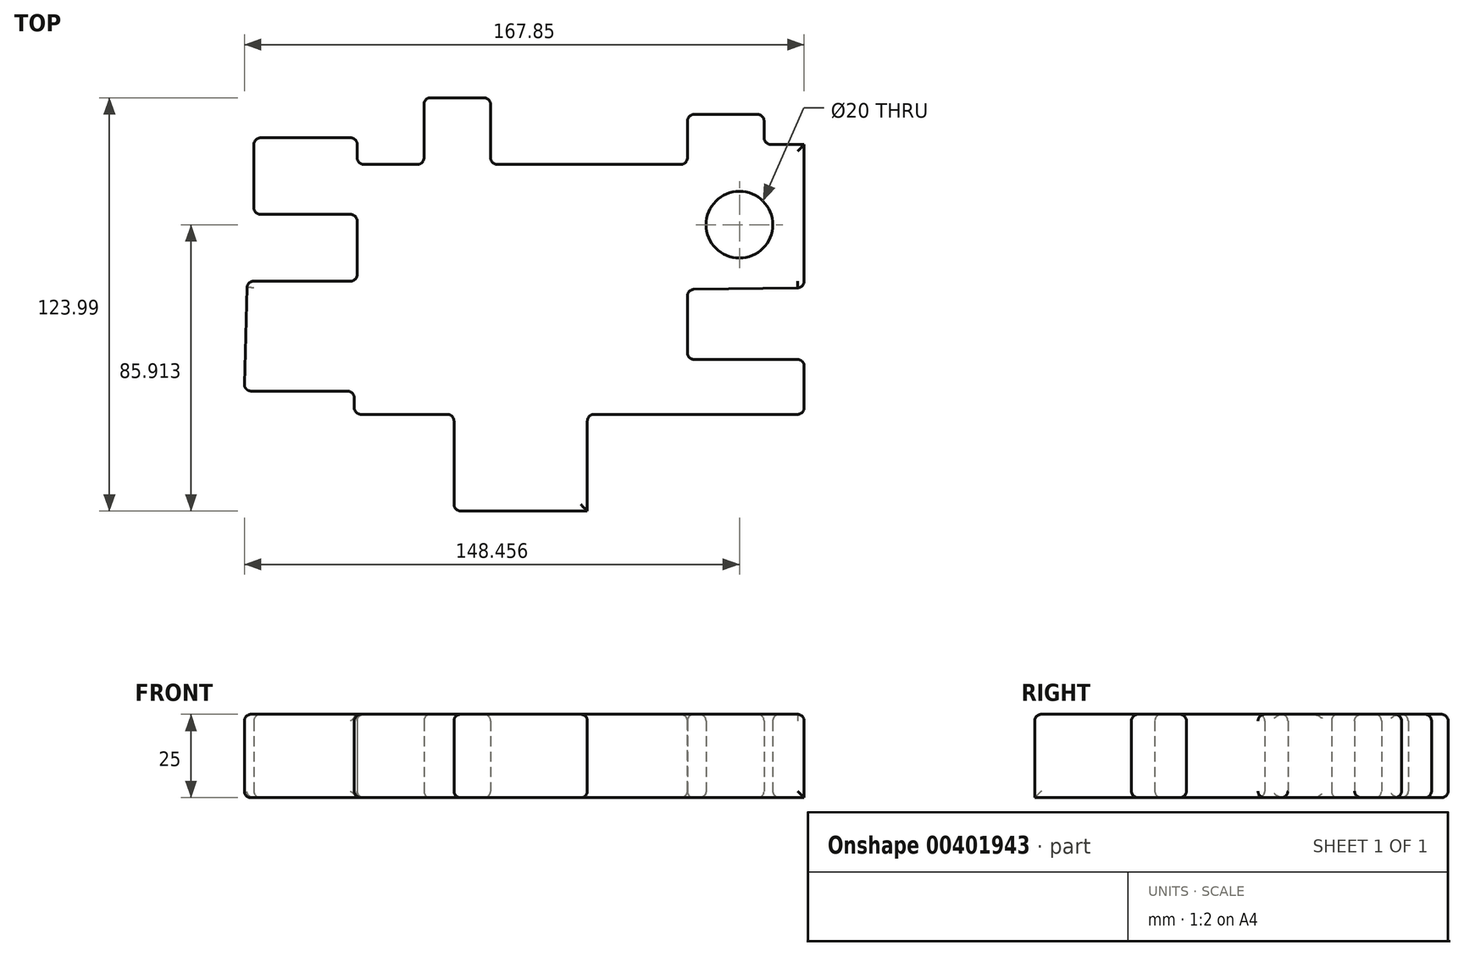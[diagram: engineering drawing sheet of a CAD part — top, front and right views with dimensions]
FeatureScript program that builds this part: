
annotation { "Feature Type Name" : "Feature", "Feature Type Description" : "" }
export const myFeature = defineFeature(function(context is Context, id is Id, definition is map)
    precondition{}
    {
        {
            var Q0;
            Q0=qCreatedBy(makeId("Top.planeOp"),FACE);
            var sketch = newSketch(context, id + "F0", { "sketchPlane" : qUnion([Q0])});
            skLineSegment(sketch, "E0.bottom", {"start": v(-24.1, 37.5) * mm, "end": v(34.9, 37.5) * mm});
            skLineSegment(sketch, "E0.top", {"start": v(-45.1, -37.49) * mm, "end": v(-35.1, -37.49) * mm});
            skLineSegment(sketch, "E1.bottom", {"start": v(-64.1, 2.5) * mm, "end": v(-97.1, 2.5) * mm});
            skLineSegment(sketch, "E1.top", {"start": v(-65.01, -30.49) * mm, "end": v(-98.01, -30.49) * mm});
            skLineSegment(sketch, "E1.right", {"start": v(-97.1, 2.5) * mm, "end": v(-98.01, -30.49) * mm});
            skLineSegment(sketch, "E2.top", {"start": v(-64.1, 37.5) * mm, "end": v(-44.1, 37.5) * mm});
            skLineSegment(sketch, "E2.left", {"start": v(-64.1, 2.5) * mm, "end": v(-64.1, 37.5) * mm});
            skLineSegment(sketch, "E3.top", {"start": v(-65.01, -37.49) * mm, "end": v(-45.1, -37.49) * mm});
            skLineSegment(sketch, "E3.left", {"start": v(-65.01, -30.49) * mm, "end": v(-65.01, -37.49) * mm});
            skLineSegment(sketch, "E4.bottom", {"start": v(34.9, -37.49) * mm, "end": v(69.9, -37.49) * mm});
            skLineSegment(sketch, "E4.top", {"start": v(34.9, -21) * mm, "end": v(69.9, -21) * mm});
            skLineSegment(sketch, "E4.right", {"start": v(69.9, -37.49) * mm, "end": v(69.9, -21) * mm});
            skLineSegment(sketch, "E5.bottom", {"start": v(34.9, 0) * mm, "end": v(69.9, 0.5) * mm});
            skLineSegment(sketch, "E6.top", {"start": v(69.9, 43.5) * mm, "end": v(57.9, 43.5) * mm});
            skLineSegment(sketch, "E6.left", {"start": v(69.9, 37.5) * mm, "end": v(69.9, 43.5) * mm});
            skLineSegment(sketch, "E7.top", {"start": v(-44.1, 57.5) * mm, "end": v(-24.1, 57.5) * mm});
            skLineSegment(sketch, "E7.left", {"start": v(-44.1, 37.5) * mm, "end": v(-44.1, 57.5) * mm});
            skLineSegment(sketch, "E7.right", {"start": v(-24.1, 37.5) * mm, "end": v(-24.1, 57.5) * mm});
            skLineSegment(sketch, "E8.top", {"start": v(34.9, 52.5) * mm, "end": v(57.9, 52.5) * mm});
            skLineSegment(sketch, "E8.left", {"start": v(34.9, 37.5) * mm, "end": v(34.9, 52.5) * mm});
            skLineSegment(sketch, "E8.right", {"start": v(57.9, 43.5) * mm, "end": v(57.9, 52.5) * mm});
            skLineSegment(sketch, "E9.top", {"start": v(-35.1, -66.49) * mm, "end": v(4.9, -66.49) * mm});
            skLineSegment(sketch, "E9.left", {"start": v(-35.1, -37.49) * mm, "end": v(-35.1, -66.49) * mm});
            skLineSegment(sketch, "E9.right", {"start": v(4.9, -37.49) * mm, "end": v(4.9, -57.49) * mm});
            skLineSegment(sketch, "E10.bottom", {"start": v(4.9, -66.49) * mm, "end": v(24.9, -66.49) * mm});
            skLineSegment(sketch, "E10.top", {"start": v(4.9, -66.49) * mm, "end": v(24.9, -66.49) * mm});
            skLineSegment(sketch, "E10.left", {"start": v(4.9, -66.49) * mm, "end": v(4.9, -66.49) * mm});
            skLineSegment(sketch, "E10.right", {"start": v(24.9, -66.49) * mm, "end": v(24.9, -66.49) * mm});
            skLineSegment(sketch, "E11.bottom", {"start": v(24.9, -57.49) * mm, "end": v(24.9, -57.49) * mm});
            skLineSegment(sketch, "E11.left", {"start": v(24.9, -57.49) * mm, "end": v(24.9, -66.49) * mm});
            skLineSegment(sketch, "E11.right", {"start": v(24.9, -57.49) * mm, "end": v(24.9, -66.49) * mm});
            skLineSegment(sketch, "E12.bottom", {"start": v(24.9, -57.49) * mm, "end": v(4.9, -57.49) * mm});
            skLineSegment(sketch, "E12.top", {"start": v(24.9, -57.49) * mm, "end": v(4.9, -57.49) * mm});
            skLineSegment(sketch, "E12.right", {"start": v(4.9, -57.49) * mm, "end": v(4.9, -57.49) * mm});
            skLineSegment(sketch, "E13.trimOffspring", {"start": v(4.9, -37.49) * mm, "end": v(34.9, -37.49) * mm});
            skLineSegment(sketch, "E14.trimOffspring", {"start": v(34.9, 0) * mm, "end": v(34.9, -21) * mm});
            skLineSegment(sketch, "E15", {"start": v(-64.1, 2.5) * mm, "end": v(-65.01, -30.49) * mm});
            skLineSegment(sketch, "E16", {"start": v(-44.1, 37.5) * mm, "end": v(-44.1, 2.5) * mm});
            skLineSegment(sketch, "E17", {"start": v(-44.1, 2.5) * mm, "end": v(-64.1, 2.5) * mm});
            skLineSegment(sketch, "E18", {"start": v(-44.1, 37.5) * mm, "end": v(-24.1, 37.5) * mm});
            skLineSegment(sketch, "E19", {"start": v(-44.1, 2.5) * mm, "end": v(-45.1, -37.49) * mm});
            skLineSegment(sketch, "E20", {"start": v(-35.1, -37.49) * mm, "end": v(4.9, -37.49) * mm});
            skLineSegment(sketch, "E21", {"start": v(4.9, -57.49) * mm, "end": v(4.9, -66.49) * mm});
            skLineSegment(sketch, "E22", {"start": v(34.4, -17.5) * mm, "end": v(34.9, -37.49) * mm});
            skLineSegment(sketch, "E23", {"start": v(34.9, 37.5) * mm, "end": v(57.9, 37.5) * mm});
            skLineSegment(sketch, "E24", {"start": v(57.9, 37.5) * mm, "end": v(57.9, 43.5) * mm});
            skLineSegment(sketch, "E25", {"start": v(34.9, 0) * mm, "end": v(34.9, 37.5) * mm});
            skLineSegment(sketch, "E26", {"start": v(57.9, 37.5) * mm, "end": v(69.9, 37.5) * mm});
            skLineSegment(sketch, "E27.bottom", {"start": v(-64.1, 22.5) * mm, "end": v(-95.1, 22.5) * mm});
            skLineSegment(sketch, "E27.top", {"start": v(-64.1, 45.5) * mm, "end": v(-95.1, 45.5) * mm});
            skLineSegment(sketch, "E27.left", {"start": v(-64.1, 22.5) * mm, "end": v(-64.1, 45.5) * mm});
            skLineSegment(sketch, "E27.right", {"start": v(-95.1, 22.5) * mm, "end": v(-95.1, 45.5) * mm});
            skLineSegment(sketch, "E28", {"start": v(-64.1, 45.5) * mm, "end": v(-64.1, 37.5) * mm});
            skLineSegment(sketch, "E29", {"start": v(-64.1, 22.5) * mm, "end": v(-64.1, 2.5) * mm});
            skPoint(sketch, "E30.orphan", {"position": v(69.9, 27.5) * mm});
            skLineSegment(sketch, "E31", {"start": v(69.9, 37.5) * mm, "end": v(69.9, 0.5) * mm});
            skCircle(sketch, "E32", {"center": v(50.5, 19.42) * mm, "radius": 10 * mm});
            skSolve(sketch);
        }
        {
            var Q0;
            Q0=makeQuery(id+"F0.imprint","IMPRINT",FACE,{"disambiguationData":[TD([[makeQuery(id+"F0.imprint","IMPRINT",EDGE,{"derivedFrom":sQuery(id+"F0.wireOp",EDGE,"E0.bottom")}),-1.0]])]});
            var Q1;
            Q1=makeQuery(id+"F0.imprint","IMPRINT",FACE,{"disambiguationData":[TD([[makeQuery(id+"F0.imprint","IMPRINT",EDGE,{"derivedFrom":sQuery(id+"F0.wireOp",EDGE,"E2.top")}),-1.0]])]});
            var Q2;
            Q2=makeQuery(id+"F0.imprint","IMPRINT",FACE,{"disambiguationData":[TD([[makeQuery(id+"F0.imprint","IMPRINT",EDGE,{"derivedFrom":sQuery(id+"F0.wireOp",EDGE,"E27.bottom")}),-1.0]])]});
            var Q3;
            Q3=makeQuery(id+"F0.imprint","IMPRINT",FACE,{"disambiguationData":[TD([[makeQuery(id+"F0.imprint","IMPRINT",EDGE,{"derivedFrom":sQuery(id+"F0.wireOp",EDGE,"E7.top")}),-1.0]])]});
            var Q4;
            Q4=makeQuery(id+"F0.imprint","IMPRINT",FACE,{"disambiguationData":[TD([[makeQuery(id+"F0.imprint","IMPRINT",EDGE,{"derivedFrom":sQuery(id+"F0.wireOp",EDGE,"E3.top")}),1.0]])]});
            var Q5;
            Q5=makeQuery(id+"F0.imprint","IMPRINT",FACE,{"disambiguationData":[TD([[makeQuery(id+"F0.imprint","IMPRINT",EDGE,{"derivedFrom":sQuery(id+"F0.wireOp",EDGE,"E1.bottom")}),1.0]])]});
            var Q6;
            Q6=makeQuery(id+"F0.imprint","IMPRINT",FACE,{"disambiguationData":[TD([[makeQuery(id+"F0.imprint","IMPRINT",EDGE,{"derivedFrom":sQuery(id+"F0.wireOp",EDGE,"E9.top")}),1.0]])]});
            var Q7;
            Q7=makeQuery(id+"F0.imprint","IMPRINT",FACE,{"disambiguationData":[TD([[makeQuery(id+"F0.imprint","IMPRINT",EDGE,{"derivedFrom":sQuery(id+"F0.wireOp",EDGE,"E10.top")}),1.0]])]});
            var Q8;
            Q8=makeQuery(id+"F0.imprint","IMPRINT",FACE,{"disambiguationData":[TD([[makeQuery(id+"F0.imprint","IMPRINT",EDGE,{"derivedFrom":sQuery(id+"F0.wireOp",EDGE,"E5.bottom")}),1.0]])]});
            var Q9;
            Q9=makeQuery(id+"F0.imprint","IMPRINT",FACE,{"disambiguationData":[TD([[makeQuery(id+"F0.imprint","IMPRINT",EDGE,{"derivedFrom":sQuery(id+"F0.wireOp",EDGE,"E8.top")}),-1.0]])]});
            var Q10;
            {var subQ0=sQuery(id+"F0.wireOp",EDGE,"E6.top");Q10=makeQuery(id+"F0.imprint","IMPRINT",FACE,{"disambiguationData":[TD([[makeQuery(id+"F0.imprint","IMPRINT",EDGE,{"derivedFrom":subQ0}),1.0]])]});}
            extrude(context, id + "F1", {"entities" : qUnion([Q0, Q1, Q2, Q3, Q4, Q5, Q6, Q7, Q8, Q9, Q10]), "depth" : 25 * mm});
        }
        {
            var Q0;
            Q0=makeQuery(id+"F1.opExtrude","CAP_EDGE",EDGE,{"disambiguationData":[OSD([sQuery(id+"F0.wireOp",EDGE,"E7.left")])],"isStart":false});
            var Q1;
            Q1=makeQuery(id+"F1.opExtrude","CAP_EDGE",EDGE,{"disambiguationData":[OSD([sQuery(id+"F0.wireOp",EDGE,"E7.top")])],"isStart":false});
            var Q2;
            Q2=makeQuery(id+"F1.opExtrude","CAP_EDGE",EDGE,{"disambiguationData":[OSD([sQuery(id+"F0.wireOp",EDGE,"E7.right")])],"isStart":false});
            var Q3;
            Q3=makeQuery(id+"F1.opExtrude","CAP_EDGE",EDGE,{"disambiguationData":[OSD([sQuery(id+"F0.wireOp",EDGE,"E0.bottom")])],"isStart":false});
            var Q4;
            Q4=makeQuery(id+"F1.opExtrude","CAP_EDGE",EDGE,{"disambiguationData":[OSD([sQuery(id+"F0.wireOp",EDGE,"E8.left")])],"isStart":false});
            var Q5;
            Q5=makeQuery(id+"F1.opExtrude","CAP_EDGE",EDGE,{"disambiguationData":[OSD([sQuery(id+"F0.wireOp",EDGE,"E8.top")])],"isStart":false});
            var Q6;
            Q6=makeQuery(id+"F1.opExtrude","CAP_EDGE",EDGE,{"disambiguationData":[OSD([sQuery(id+"F0.wireOp",EDGE,"E8.right")])],"isStart":false});
            var Q7;
            Q7=makeQuery(id+"F1.opExtrude","CAP_EDGE",EDGE,{"disambiguationData":[OSD([sQuery(id+"F0.wireOp",EDGE,"E6.top")])],"isStart":false});
            var Q8;
            Q8=makeQuery(id+"F1.opExtrude","CAP_EDGE",EDGE,{"disambiguationData":[OSD([sQuery(id+"F0.wireOp",EDGE,"E6.left")])],"isStart":false});
            var Q9;
            Q9=makeQuery(id+"F1.opExtrude","CAP_EDGE",EDGE,{"disambiguationData":[OSD([sQuery(id+"F0.wireOp",EDGE,"E5.right")])],"isStart":false});
            var Q10;
            Q10=makeQuery(id+"F1.opExtrude","CAP_EDGE",EDGE,{"disambiguationData":[OSD([sQuery(id+"F0.wireOp",EDGE,"E5.bottom")])],"isStart":false});
            var Q11;
            Q11=makeQuery(id+"F1.opExtrude","CAP_EDGE",EDGE,{"disambiguationData":[OSD([sQuery(id+"F0.wireOp",EDGE,"E14.trimOffspring")])],"isStart":false});
            var Q12;
            Q12=makeQuery(id+"F1.opExtrude","CAP_EDGE",EDGE,{"disambiguationData":[OSD([sQuery(id+"F0.wireOp",EDGE,"E4.top")])],"isStart":false});
            var Q13;
            Q13=makeQuery(id+"F1.opExtrude","CAP_EDGE",EDGE,{"disambiguationData":[OSD([sQuery(id+"F0.wireOp",EDGE,"E4.right")])],"isStart":false});
            var Q14;
            Q14=makeQuery(id+"F1.opExtrude","CAP_EDGE",EDGE,{"disambiguationData":[OSD([sQuery(id+"F0.wireOp",EDGE,"E4.bottom"),sQuery(id+"F0.wireOp",EDGE,"E13.trimOffspring")])],"isStart":false});
            var Q15;
            Q15=makeQuery(id+"F1.opExtrude","CAP_EDGE",EDGE,{"disambiguationData":[OSD([sQuery(id+"F0.wireOp",EDGE,"E9.right")])],"isStart":false});
            var Q16;
            Q16=makeQuery(id+"F1.opExtrude","CAP_EDGE",EDGE,{"disambiguationData":[OSD([sQuery(id+"F0.wireOp",EDGE,"E12.top")])],"isStart":false});
            var Q17;
            Q17=makeQuery(id+"F1.opExtrude","CAP_EDGE",EDGE,{"disambiguationData":[OSD([sQuery(id+"F0.wireOp",EDGE,"E11.right")])],"isStart":false});
            var Q18;
            Q18=makeQuery(id+"F1.opExtrude","CAP_EDGE",EDGE,{"disambiguationData":[OSD([sQuery(id+"F0.wireOp",EDGE,"E9.top"),sQuery(id+"F0.wireOp",EDGE,"E10.top")])],"isStart":false});
            var Q19;
            Q19=makeQuery(id+"F1.opExtrude","CAP_EDGE",EDGE,{"disambiguationData":[OSD([sQuery(id+"F0.wireOp",EDGE,"E9.left")])],"isStart":false});
            var Q20;
            Q20=makeQuery(id+"F1.opExtrude","CAP_EDGE",EDGE,{"disambiguationData":[OSD([sQuery(id+"F0.wireOp",EDGE,"E0.top"),sQuery(id+"F0.wireOp",EDGE,"E3.top")])],"isStart":false});
            var Q21;
            Q21=makeQuery(id+"F1.opExtrude","CAP_EDGE",EDGE,{"disambiguationData":[OSD([sQuery(id+"F0.wireOp",EDGE,"E3.left")])],"isStart":false});
            var Q22;
            Q22=makeQuery(id+"F1.opExtrude","CAP_EDGE",EDGE,{"disambiguationData":[OSD([sQuery(id+"F0.wireOp",EDGE,"E1.top")])],"isStart":false});
            var Q23;
            Q23=makeQuery(id+"F1.opExtrude","CAP_EDGE",EDGE,{"disambiguationData":[OSD([sQuery(id+"F0.wireOp",EDGE,"E1.right")])],"isStart":false});
            var Q24;
            Q24=makeQuery(id+"F1.opExtrude","CAP_EDGE",EDGE,{"disambiguationData":[OSD([sQuery(id+"F0.wireOp",EDGE,"E1.bottom")])],"isStart":false});
            var Q25;
            Q25=makeQuery(id+"F1.opExtrude","CAP_EDGE",EDGE,{"disambiguationData":[OSD([sQuery(id+"F0.wireOp",EDGE,"E29")])],"isStart":false});
            var Q26;
            Q26=makeQuery(id+"F1.opExtrude","CAP_EDGE",EDGE,{"disambiguationData":[OSD([sQuery(id+"F0.wireOp",EDGE,"E27.bottom")])],"isStart":false});
            var Q27;
            Q27=makeQuery(id+"F1.opExtrude","CAP_EDGE",EDGE,{"disambiguationData":[OSD([sQuery(id+"F0.wireOp",EDGE,"E27.right")])],"isStart":false});
            var Q28;
            Q28=makeQuery(id+"F1.opExtrude","CAP_EDGE",EDGE,{"disambiguationData":[OSD([sQuery(id+"F0.wireOp",EDGE,"E27.top")])],"isStart":false});
            var Q29;
            Q29=makeQuery(id+"F1.opExtrude","CAP_EDGE",EDGE,{"disambiguationData":[OSD([sQuery(id+"F0.wireOp",EDGE,"E28")])],"isStart":false});
            var Q30;
            Q30=makeQuery(id+"F1.opExtrude","CAP_EDGE",EDGE,{"disambiguationData":[OSD([sQuery(id+"F0.wireOp",EDGE,"E2.top")])],"isStart":false});
            var Q31;
            Q31=makeQuery(id+"F1.opExtrude","CAP_EDGE",EDGE,{"disambiguationData":[OSD([sQuery(id+"F0.wireOp",EDGE,"E31")])],"isStart":false});
            var Q32;
            Q32=makeQuery(id+"F1.opExtrude","CAP_EDGE",EDGE,{"disambiguationData":[OSD([sQuery(id+"F0.wireOp",EDGE,"E7.top")])],"isStart":true});
            var Q33;
            Q33=makeQuery(id+"F1.opExtrude","CAP_EDGE",EDGE,{"disambiguationData":[OSD([sQuery(id+"F0.wireOp",EDGE,"E7.right")])],"isStart":true});
            var Q34;
            Q34=makeQuery(id+"F1.opExtrude","CAP_EDGE",EDGE,{"disambiguationData":[OSD([sQuery(id+"F0.wireOp",EDGE,"E0.bottom")])],"isStart":true});
            var Q35;
            Q35=makeQuery(id+"F1.opExtrude","CAP_EDGE",EDGE,{"disambiguationData":[OSD([sQuery(id+"F0.wireOp",EDGE,"E8.top")])],"isStart":true});
            var Q36;
            Q36=makeQuery(id+"F1.opExtrude","CAP_EDGE",EDGE,{"disambiguationData":[OSD([sQuery(id+"F0.wireOp",EDGE,"E8.left")])],"isStart":true});
            var Q37;
            Q37=makeQuery(id+"F1.opExtrude","CAP_EDGE",EDGE,{"disambiguationData":[OSD([sQuery(id+"F0.wireOp",EDGE,"E8.right")])],"isStart":true});
            var Q38;
            Q38=makeQuery(id+"F1.opExtrude","CAP_EDGE",EDGE,{"disambiguationData":[OSD([sQuery(id+"F0.wireOp",EDGE,"E6.top")])],"isStart":true});
            var Q39;
            Q39=makeQuery(id+"F1.opExtrude","CAP_EDGE",EDGE,{"disambiguationData":[OSD([sQuery(id+"F0.wireOp",EDGE,"E7.left")])],"isStart":true});
            var Q40;
            Q40=makeQuery(id+"F1.opExtrude","CAP_EDGE",EDGE,{"disambiguationData":[OSD([sQuery(id+"F0.wireOp",EDGE,"E2.top")])],"isStart":true});
            var Q41;
            Q41=makeQuery(id+"F1.opExtrude","CAP_EDGE",EDGE,{"disambiguationData":[OSD([sQuery(id+"F0.wireOp",EDGE,"E27.top")])],"isStart":true});
            var Q42;
            Q42=makeQuery(id+"F1.opExtrude","CAP_EDGE",EDGE,{"disambiguationData":[OSD([sQuery(id+"F0.wireOp",EDGE,"E27.right")])],"isStart":true});
            var Q43;
            Q43=makeQuery(id+"F1.opExtrude","CAP_EDGE",EDGE,{"disambiguationData":[OSD([sQuery(id+"F0.wireOp",EDGE,"E27.bottom")])],"isStart":true});
            var Q44;
            Q44=makeQuery(id+"F1.opExtrude","CAP_EDGE",EDGE,{"disambiguationData":[OSD([sQuery(id+"F0.wireOp",EDGE,"E29")])],"isStart":true});
            var Q45;
            Q45=makeQuery(id+"F1.opExtrude","CAP_EDGE",EDGE,{"disambiguationData":[OSD([sQuery(id+"F0.wireOp",EDGE,"E1.bottom")])],"isStart":true});
            var Q46;
            Q46=makeQuery(id+"F1.opExtrude","SWEPT_EDGE",EDGE,{"disambiguationData":[OSD([sQuery(id+"F0.wireOp",EDGE,"E1.top"),sQuery(id+"F0.wireOp",EDGE,"E1.right")])]});
            var Q47;
            Q47=makeQuery(id+"F1.opExtrude","CAP_EDGE",EDGE,{"disambiguationData":[OSD([sQuery(id+"F0.wireOp",EDGE,"E9.right")])],"isStart":true});
            var Q48;
            Q48=makeQuery(id+"F1.opExtrude","CAP_EDGE",EDGE,{"disambiguationData":[OSD([sQuery(id+"F0.wireOp",EDGE,"E12.top")])],"isStart":true});
            var Q49;
            Q49=makeQuery(id+"F1.opExtrude","CAP_EDGE",EDGE,{"disambiguationData":[OSD([sQuery(id+"F0.wireOp",EDGE,"E4.bottom"),sQuery(id+"F0.wireOp",EDGE,"E13.trimOffspring")])],"isStart":true});
            var Q50;
            Q50=makeQuery(id+"F1.opExtrude","CAP_EDGE",EDGE,{"disambiguationData":[OSD([sQuery(id+"F0.wireOp",EDGE,"E4.top")])],"isStart":true});
            var Q51;
            Q51=makeQuery(id+"F1.opExtrude","CAP_EDGE",EDGE,{"disambiguationData":[OSD([sQuery(id+"F0.wireOp",EDGE,"E14.trimOffspring")])],"isStart":true});
            var Q52;
            Q52=makeQuery(id+"F1.opExtrude","CAP_EDGE",EDGE,{"disambiguationData":[OSD([sQuery(id+"F0.wireOp",EDGE,"E5.bottom")])],"isStart":true});
            var Q53;
            Q53=makeQuery(id+"F1.opExtrude","SWEPT_EDGE",EDGE,{"disambiguationData":[OSD([sQuery(id+"F0.wireOp",EDGE,"E7.top"),sQuery(id+"F0.wireOp",EDGE,"E7.right")])]});
            var Q54;
            Q54=makeQuery(id+"F1.opExtrude","SWEPT_EDGE",EDGE,{"disambiguationData":[OSD([sQuery(id+"F0.wireOp",EDGE,"E7.top"),sQuery(id+"F0.wireOp",EDGE,"E7.left")])]});
            var Q55;
            Q55=makeQuery(id+"F1.opExtrude","SWEPT_FACE",FACE,{"disambiguationData":[OSD([sQuery(id+"F0.wireOp",EDGE,"E27.top")])]});
            var Q56;
            Q56=makeQuery(id+"F1.opExtrude","SWEPT_EDGE",EDGE,{"disambiguationData":[OSD([sQuery(id+"F0.wireOp",EDGE,"E27.top"),sQuery(id+"F0.wireOp",EDGE,"E28")])]});
            var Q57;
            Q57=makeQuery(id+"F1.opExtrude","SWEPT_EDGE",EDGE,{"disambiguationData":[OSD([sQuery(id+"F0.wireOp",EDGE,"E27.top"),sQuery(id+"F0.wireOp",EDGE,"E27.right")])]});
            var Q58;
            Q58=makeQuery(id+"F1.opExtrude","SWEPT_EDGE",EDGE,{"disambiguationData":[OSD([sQuery(id+"F0.wireOp",EDGE,"E8.top"),sQuery(id+"F0.wireOp",EDGE,"E8.right")])]});
            var Q59;
            Q59=makeQuery(id+"F1.opExtrude","SWEPT_EDGE",EDGE,{"disambiguationData":[OSD([sQuery(id+"F0.wireOp",EDGE,"E8.top"),sQuery(id+"F0.wireOp",EDGE,"E8.left")])]});
            var Q60;
            Q60=makeQuery(id+"F1.opExtrude","SWEPT_EDGE",EDGE,{"disambiguationData":[OSD([sQuery(id+"F0.wireOp",EDGE,"E27.bottom"),sQuery(id+"F0.wireOp",EDGE,"E27.right")])]});
            var Q61;
            Q61=makeQuery(id+"F1.opExtrude","SWEPT_EDGE",EDGE,{"disambiguationData":[OSD([sQuery(id+"F0.wireOp",EDGE,"E1.bottom"),sQuery(id+"F0.wireOp",EDGE,"E15"),sQuery(id+"F0.wireOp",EDGE,"E17"),sQuery(id+"F0.wireOp",EDGE,"E29")])]});
            var Q62;
            Q62=makeQuery(id+"F1.opExtrude","SWEPT_EDGE",EDGE,{"disambiguationData":[OSD([sQuery(id+"F0.wireOp",EDGE,"E1.bottom"),sQuery(id+"F0.wireOp",EDGE,"E1.right")])]});
            var Q63;
            Q63=makeQuery(id+"F1.opExtrude","CAP_EDGE",EDGE,{"disambiguationData":[OSD([sQuery(id+"F0.wireOp",EDGE,"E1.top")])],"isStart":true});
            var Q64;
            Q64=makeQuery(id+"F1.opExtrude","CAP_EDGE",EDGE,{"disambiguationData":[OSD([sQuery(id+"F0.wireOp",EDGE,"E3.left")])],"isStart":true});
            var Q65;
            Q65=makeQuery(id+"F1.opExtrude","CAP_EDGE",EDGE,{"disambiguationData":[OSD([sQuery(id+"F0.wireOp",EDGE,"E0.top"),sQuery(id+"F0.wireOp",EDGE,"E3.top")])],"isStart":true});
            var Q66;
            Q66=makeQuery(id+"F1.opExtrude","SWEPT_EDGE",EDGE,{"disambiguationData":[OSD([sQuery(id+"F0.wireOp",EDGE,"E3.top"),sQuery(id+"F0.wireOp",EDGE,"E3.left")])]});
            var Q67;
            Q67=makeQuery(id+"F1.opExtrude","CAP_EDGE",EDGE,{"disambiguationData":[OSD([sQuery(id+"F0.wireOp",EDGE,"E9.left")])],"isStart":true});
            var Q68;
            Q68=makeQuery(id+"F1.opExtrude","SWEPT_EDGE",EDGE,{"disambiguationData":[OSD([sQuery(id+"F0.wireOp",EDGE,"E6.top"),sQuery(id+"F0.wireOp",EDGE,"E8.right"),sQuery(id+"F0.wireOp",EDGE,"E24")])]});
            var Q69;
            Q69=makeQuery(id+"F1.opExtrude","SWEPT_EDGE",EDGE,{"disambiguationData":[OSD([sQuery(id+"F0.wireOp",EDGE,"E4.top"),sQuery(id+"F0.wireOp",EDGE,"E14.trimOffspring")])]});
            var Q70;
            Q70=makeQuery(id+"F1.opExtrude","SWEPT_EDGE",EDGE,{"disambiguationData":[OSD([sQuery(id+"F0.wireOp",EDGE,"E5.bottom"),sQuery(id+"F0.wireOp",EDGE,"E31")])]});
            var Q71;
            Q71=makeQuery(id+"F1.opExtrude","SWEPT_EDGE",EDGE,{"disambiguationData":[OSD([sQuery(id+"F0.wireOp",EDGE,"E11.right"),sQuery(id+"F0.wireOp",EDGE,"E12.top")])]});
            var Q72;
            Q72=makeQuery(id+"F1.opExtrude","SWEPT_EDGE",EDGE,{"disambiguationData":[OSD([sQuery(id+"F0.wireOp",EDGE,"E10.top"),sQuery(id+"F0.wireOp",EDGE,"E11.right")])]});
            var Q73;
            Q73=makeQuery(id+"F1.opExtrude","SWEPT_EDGE",EDGE,{"disambiguationData":[OSD([sQuery(id+"F0.wireOp",EDGE,"E4.bottom"),sQuery(id+"F0.wireOp",EDGE,"E4.right")])]});
            var Q74;
            Q74=makeQuery(id+"F1.opExtrude","SWEPT_EDGE",EDGE,{"disambiguationData":[OSD([sQuery(id+"F0.wireOp",EDGE,"E4.top"),sQuery(id+"F0.wireOp",EDGE,"E4.right")])]});
            var Q75;
            Q75=makeQuery(id+"F1.opExtrude","SWEPT_EDGE",EDGE,{"disambiguationData":[OSD([sQuery(id+"F0.wireOp",EDGE,"E9.top"),sQuery(id+"F0.wireOp",EDGE,"E9.left")])]});
            var Q76;
            Q76=makeQuery(id+"F1.opExtrude","SWEPT_EDGE",EDGE,{"disambiguationData":[OSD([sQuery(id+"F0.wireOp",EDGE,"E0.top"),sQuery(id+"F0.wireOp",EDGE,"E9.left"),sQuery(id+"F0.wireOp",EDGE,"E20")])]});
            var Q77;
            Q77=makeQuery(id+"F1.opExtrude","SWEPT_EDGE",EDGE,{"disambiguationData":[OSD([sQuery(id+"F0.wireOp",EDGE,"E27.bottom"),sQuery(id+"F0.wireOp",EDGE,"E27.left"),sQuery(id+"F0.wireOp",EDGE,"E29")])]});
            var Q78;
            Q78=makeQuery(id+"F1.opExtrude","SWEPT_EDGE",EDGE,{"disambiguationData":[OSD([sQuery(id+"F0.wireOp",EDGE,"E9.right"),sQuery(id+"F0.wireOp",EDGE,"E13.trimOffspring"),sQuery(id+"F0.wireOp",EDGE,"E20")])]});
            var Q79;
            Q79=makeQuery(id+"F1.opExtrude","SWEPT_EDGE",EDGE,{"disambiguationData":[OSD([sQuery(id+"F0.wireOp",EDGE,"E5.bottom"),sQuery(id+"F0.wireOp",EDGE,"E14.trimOffspring"),sQuery(id+"F0.wireOp",EDGE,"E25")])]});
            var Q80;
            Q80=makeQuery(id+"F1.opExtrude","SWEPT_EDGE",EDGE,{"disambiguationData":[OSD([sQuery(id+"F0.wireOp",EDGE,"E0.bottom"),sQuery(id+"F0.wireOp",EDGE,"E8.left"),sQuery(id+"F0.wireOp",EDGE,"E23"),sQuery(id+"F0.wireOp",EDGE,"E25")])]});
            var Q81;
            Q81=makeQuery(id+"F1.opExtrude","SWEPT_EDGE",EDGE,{"disambiguationData":[OSD([sQuery(id+"F0.wireOp",EDGE,"E0.bottom"),sQuery(id+"F0.wireOp",EDGE,"E7.right"),sQuery(id+"F0.wireOp",EDGE,"E18")])]});
            var Q82;
            Q82=makeQuery(id+"F1.opExtrude","SWEPT_EDGE",EDGE,{"disambiguationData":[OSD([sQuery(id+"F0.wireOp",EDGE,"E2.top"),sQuery(id+"F0.wireOp",EDGE,"E7.left"),sQuery(id+"F0.wireOp",EDGE,"E16"),sQuery(id+"F0.wireOp",EDGE,"E18")])]});
            var Q83;
            Q83=makeQuery(id+"F1.opExtrude","SWEPT_EDGE",EDGE,{"disambiguationData":[OSD([sQuery(id+"F0.wireOp",EDGE,"E2.top"),sQuery(id+"F0.wireOp",EDGE,"E27.left"),sQuery(id+"F0.wireOp",EDGE,"E28")])]});
            var Q84;
            Q84=makeQuery(id+"F1.opExtrude","SWEPT_EDGE",EDGE,{"disambiguationData":[OSD([sQuery(id+"F0.wireOp",EDGE,"E1.top"),sQuery(id+"F0.wireOp",EDGE,"E3.left"),sQuery(id+"F0.wireOp",EDGE,"E15")])]});
            var Q85;
            Q85=makeQuery(id+"F1.opExtrude","CAP_EDGE",EDGE,{"disambiguationData":[OSD([sQuery(id+"F0.wireOp",EDGE,"E1.right")])],"isStart":true});
            var Q86;
            Q86=makeQuery(id+"F1.opExtrude","CAP_EDGE",EDGE,{"disambiguationData":[OSD([sQuery(id+"F0.wireOp",EDGE,"E32")])],"isStart":true});
            var Q87;
            Q87=makeQuery(id+"F1.opExtrude","CAP_EDGE",EDGE,{"disambiguationData":[OSD([sQuery(id+"F0.wireOp",EDGE,"E32")])],"isStart":false});
            fillet(context, id + "F2", {"entities" : qUnion([Q0, Q1, Q2, Q3, Q4, Q5, Q6, Q7, Q8, Q9, Q10, Q11, Q12, Q13, Q14, Q15, Q16, Q17, Q18, Q19, Q20, Q21, Q22, Q23, Q24, Q25, Q26, Q27, Q28, Q29, Q30, Q31, Q32, Q33, Q34, Q35, Q36, Q37, Q38, Q39, Q40, Q41, Q42, Q43, Q44, Q45, Q46, Q47, Q48, Q49, Q50, Q51, Q52, Q53, Q54, Q55, Q56, Q57, Q58, Q59, Q60, Q61, Q62, Q63, Q64, Q65, Q66, Q67, Q68, Q69, Q70, Q71, Q72, Q73, Q74, Q75, Q76, Q77, Q78, Q79, Q80, Q81, Q82, Q83, Q84, Q85, Q86, Q87]), "radius" : 2 * mm, "tangentPropagation" : true, "allowEdgeOverflow" : false});
        }
    });
